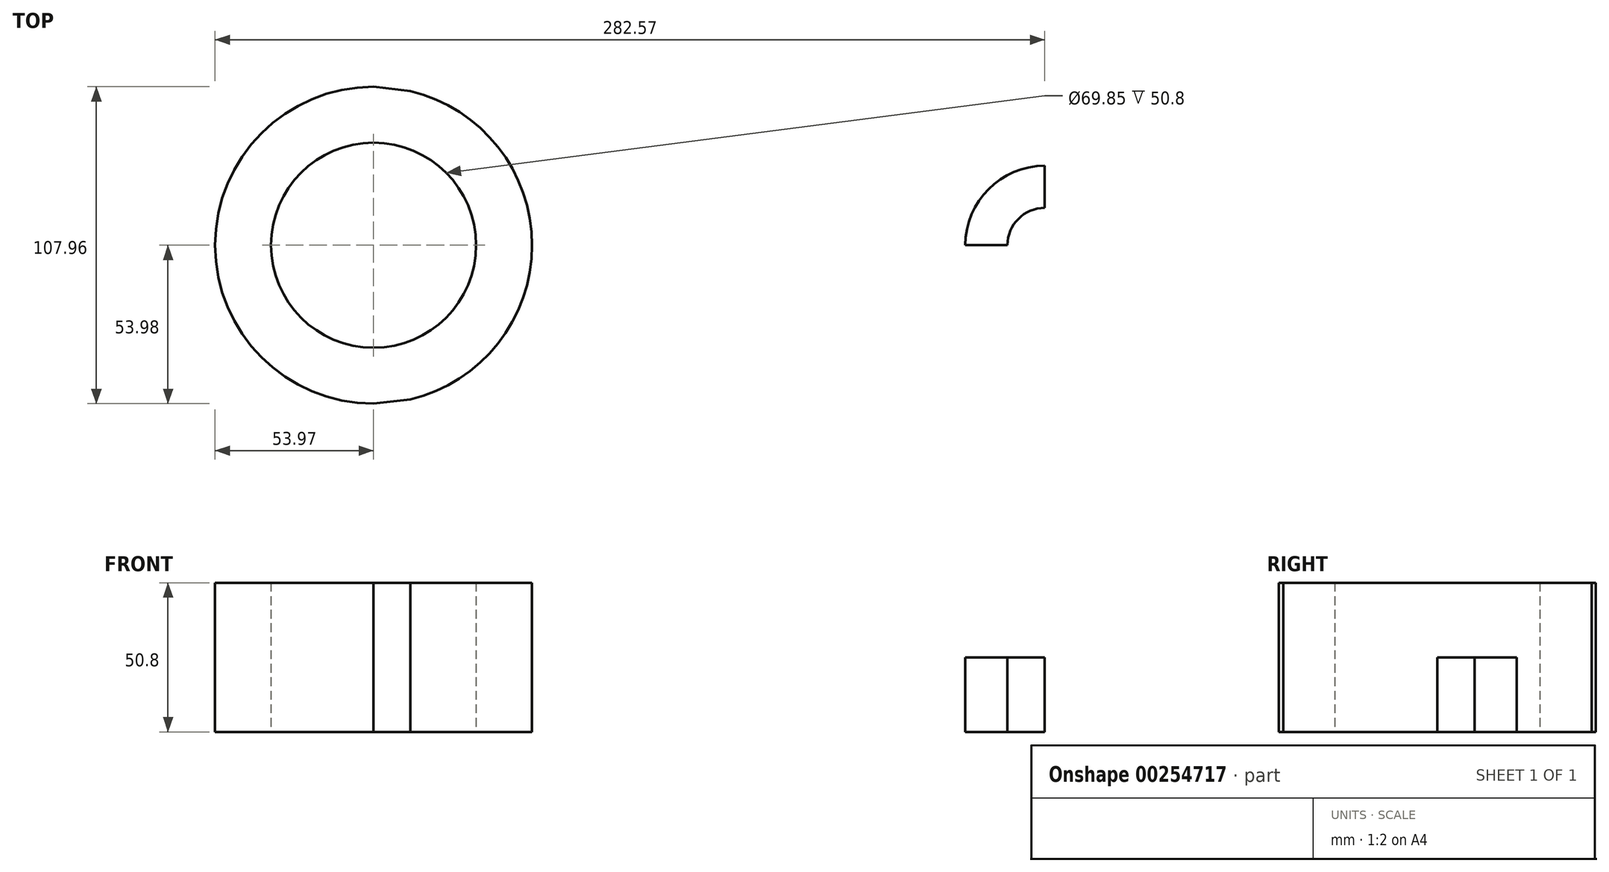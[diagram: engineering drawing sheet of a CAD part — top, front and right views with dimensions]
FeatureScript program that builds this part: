
annotation { "Feature Type Name" : "Feature", "Feature Type Description" : "" }
export const myFeature = defineFeature(function(context is Context, id is Id, definition is map)
    precondition{}
    {
        {
            var Q0;
            Q0=qCreatedBy(makeId("Top.planeOp"),FACE);
            var sketch = newSketch(context, id + "F0", { "sketchPlane" : qUnion([Q0])});
            skCircle(sketch, "E0", {"center": v(-228.6, 0) * mm, "radius": 34.93 * mm});
            skCircle(sketch, "E1", {"center": v(-228.6, 0) * mm, "radius": 53.98 * mm});
            skLineSegment(sketch, "E2", {"start": v(-228.6, 0) * mm, "end": v(-228.6, 34.92) * mm});
            skCircle(sketch, "E3", {"center": v(0, 0) * mm, "radius": 12.7 * mm});
            skCircle(sketch, "E4", {"center": v(0, 0) * mm, "radius": 27.05 * mm});
            skLineSegment(sketch, "E5", {"start": v(0, 0) * mm, "end": v(0, 27.05) * mm});
            skLineSegment(sketch, "E6", {"start": v(0, 27.05) * mm, "end": v(-228.6, 53.97) * mm});
            skLineSegment(sketch, "E7", {"start": v(-228.6, 0) * mm, "end": v(-228.6, -53.98) * mm});
            skCircle(sketch, "E8", {"center": v(-63.5, 0) * mm, "radius": 19.05 * mm});
            skCircle(sketch, "E9", {"center": v(-152.4, 0) * mm, "radius": 19.05 * mm});
            skLineSegment(sketch, "E10", {"start": v(-152.4, 19.05) * mm, "end": v(-63.5, 19.05) * mm});
            skLineSegment(sketch, "E11", {"start": v(-63.5, -19.05) * mm, "end": v(-152.4, -19.05) * mm});
            skLineSegment(sketch, "E12", {"start": v(-228.6, -53.98) * mm, "end": v(0, -27.24) * mm});
            skLineSegment(sketch, "E13", {"start": v(-228.6, 0) * mm, "end": v(-152.4, 0) * mm});
            skLineSegment(sketch, "E14", {"start": v(-152.4, 0) * mm, "end": v(-63.5, 0) * mm});
            skLineSegment(sketch, "E15", {"start": v(-63.5, 0) * mm, "end": v(0, 0) * mm});
            skSolve(sketch);
        }
        {
            var Q0;
            {var subQ8=sQuery(id+"F0.wireOp",EDGE,"E0");var subQ9=makeQuery(id+"F0.imprint","INTERSECT",VERTEX,{"derivedFrom":[subQ8,sQuery(id+"F0.wireOp",EDGE,"E2")]});Q0=makeQuery(id+"F0.imprint","IMPRINT",FACE,{"disambiguationData":[TD([[makeQuery(id+"F0.imprint","IMPRINT",EDGE,{"disambiguationData":[TD([[subQ9,1.0]])],"derivedFrom":subQ8}),-1.0]])]});}
            var Q1;
            {var subQ5=sQuery(id+"F0.wireOp",EDGE,"E13");var subQ6=sQuery(id+"F0.wireOp",EDGE,"E0");var subQ7=makeQuery(id+"F0.imprint","INTERSECT",VERTEX,{"derivedFrom":[subQ6,subQ5]});Q1=makeQuery(id+"F0.imprint","IMPRINT",FACE,{"disambiguationData":[TD([[makeQuery(id+"F0.imprint","IMPRINT",EDGE,{"disambiguationData":[TD([[subQ7,1.0]])],"derivedFrom":subQ6}),-1.0]])]});}
            extrude(context, id + "F1", {"entities" : qUnion([Q0, Q1]), "depth" : 50.8 * mm});
        }
        {
            var Q0;
            {var subQ0=sQuery(id+"F0.wireOp",EDGE,"E5");var subQ1=sQuery(id+"F0.wireOp",EDGE,"E3");var subQ2=makeQuery(id+"F0.imprint","INTERSECT",VERTEX,{"derivedFrom":[subQ1,subQ0]});Q0=makeQuery(id+"F0.imprint","IMPRINT",FACE,{"disambiguationData":[TD([[makeQuery(id+"F0.imprint","IMPRINT",EDGE,{"disambiguationData":[TD([[subQ2,-1.0]])],"derivedFrom":subQ1}),-1.0]])]});}
            extrude(context, id + "F2", {"entities" : qUnion([Q0]), "depth" : 25.4 * mm});
        }
    });
